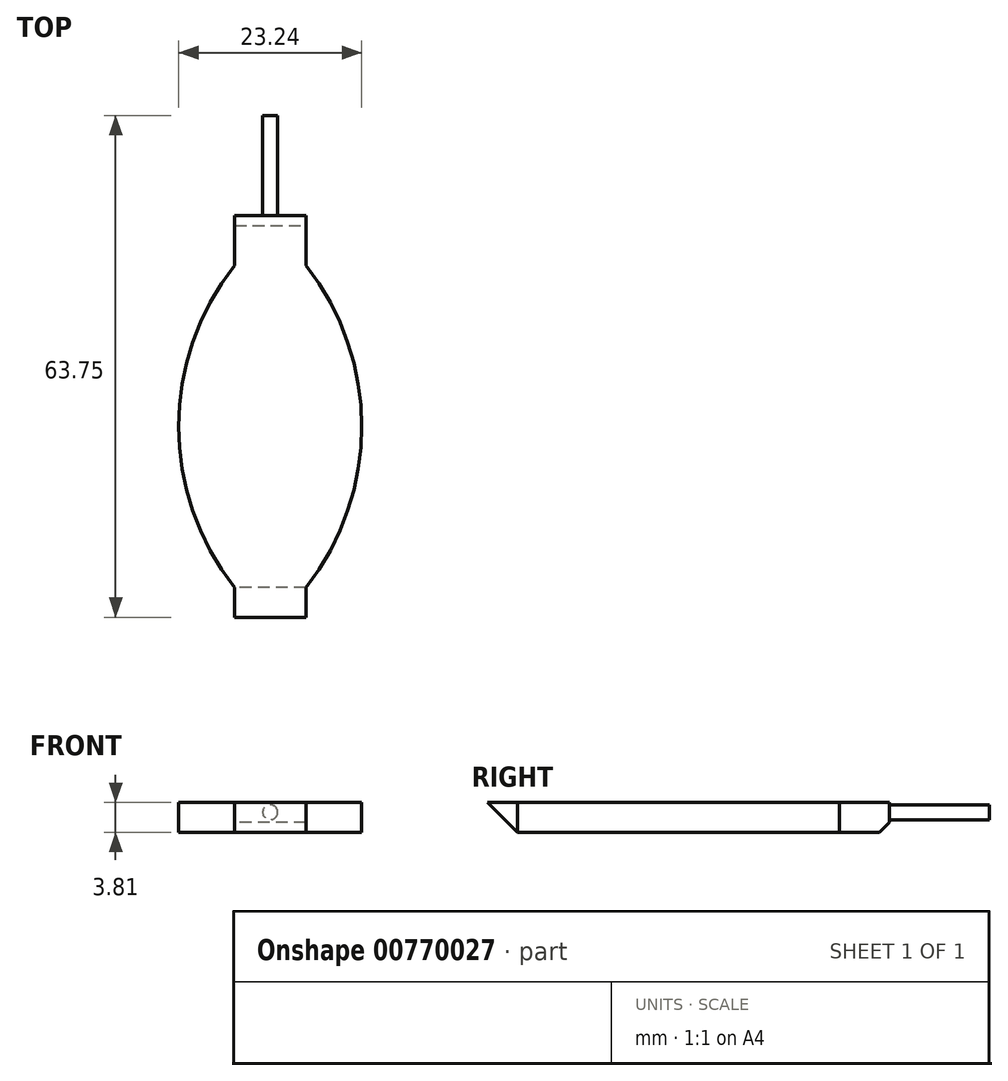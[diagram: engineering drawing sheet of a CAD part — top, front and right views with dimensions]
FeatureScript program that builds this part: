
annotation { "Feature Type Name" : "Feature", "Feature Type Description" : "" }
export const myFeature = defineFeature(function(context is Context, id is Id, definition is map)
    precondition{}
    {
        {
            var Q0;
            Q0=qCreatedBy(makeId("Top.planeOp"),FACE);
            var sketch = newSketch(context, id + "F0", { "sketchPlane" : qUnion([Q0])});
            skLineSegment(sketch, "E0.top", {"start": v(-4.53, -2.42) * mm, "end": v(4.53, -2.42) * mm});
            skPoint(sketch, "E0.middle", {"position": v(0, 0) * mm});
            skLineSegment(sketch, "E1", {"start": v(-4.53, -43.3) * mm, "end": v(4.53, -43.3) * mm});
            skArc(sketch, "E2", {"start": v(4.53, -43.3) * mm, "mid": v(11.62, -22.86) * mm, "end": v(4.53, -2.42) * mm});
            skArc(sketch, "E3", {"start": v(-4.53, -2.42) * mm, "mid": v(-11.62, -22.86) * mm, "end": v(-4.53, -43.3) * mm});
            skSolve(sketch);
        }
        {
            var Q0;
            Q0=qSketchRegion(id+"F0",true);
            extrude(context, id + "F1", {"entities" : qUnion([Q0]), "depth" : 3.8 * mm, "offsetDistance" : 25.4 * mm});
        }
        {
            var Q0;
            Q0=makeQuery(id+"F1.opExtrude","SWEPT_FACE",FACE,{"disambiguationData":[OSD([sQuery(id+"F0.wireOp",EDGE,"E0.top")])]});
            var sketch = newSketch(context, id + "F2", { "sketchPlane" : qUnion([Q0])});
            skLineSegment(sketch, "E4.bottom", {"start": v(-4.53, 3.81) * mm, "end": v(4.53, 3.81) * mm});
            skLineSegment(sketch, "E4.top", {"start": v(-4.53, 0) * mm, "end": v(4.53, 0) * mm});
            skLineSegment(sketch, "E4.left", {"start": v(-4.53, 3.81) * mm, "end": v(-4.53, 0) * mm});
            skLineSegment(sketch, "E4.right", {"start": v(4.53, 3.81) * mm, "end": v(4.53, 0) * mm});
            skSolve(sketch);
        }
        {
            var Q0;
            Q0=qSketchRegion(id+"F2",true);
            extrude(context, id + "F3", {"entities" : qUnion([Q0]), "operationType" : NewBodyOperationType.ADD, "depth" : 6.35 * mm, "offsetDistance" : 25.4 * mm});
        }
        {
            var Q0;
            Q0=makeQuery(id+"F3.opExtrude","CAP_EDGE",EDGE,{"disambiguationData":[OSD([sQuery(id+"F2.wireOp",EDGE,"E4.top")])],"isStart":false});
            chamfer(context, id + "F4", {"entities" : qUnion([Q0]), "width" : 1.27 * mm, "tangentPropagation" : true});
        }
        {
            var Q0;
            Q0=makeQuery(id+"F1.opExtrude","SWEPT_FACE",FACE,{"disambiguationData":[OSD([sQuery(id+"F0.wireOp",EDGE,"E1")])]});
            var sketch = newSketch(context, id + "F5", { "sketchPlane" : qUnion([Q0])});
            skLineSegment(sketch, "E5.bottom", {"start": v(-4.53, 3.81) * mm, "end": v(4.53, 3.81) * mm});
            skLineSegment(sketch, "E5.top", {"start": v(-4.53, 0) * mm, "end": v(4.53, 0) * mm});
            skLineSegment(sketch, "E5.left", {"start": v(-4.53, 3.81) * mm, "end": v(-4.53, 0) * mm});
            skLineSegment(sketch, "E5.right", {"start": v(4.53, 3.81) * mm, "end": v(4.53, 0) * mm});
            skSolve(sketch);
        }
        {
            var Q0;
            Q0=qSketchRegion(id+"F5",true);
            extrude(context, id + "F6", {"entities" : qUnion([Q0]), "operationType" : NewBodyOperationType.ADD, "depth" : 5.08 * mm, "offsetDistance" : 25.4 * mm});
        }
        {
            var Q0;
            Q0=makeQuery(id+"F6.opExtrude","CAP_EDGE",EDGE,{"disambiguationData":[OSD([sQuery(id+"F5.wireOp",EDGE,"E5.top")])],"isStart":false});
            chamfer(context, id + "F7", {"entities" : qUnion([Q0]), "width" : 5.08 * mm, "tangentPropagation" : true});
        }
        {
            var Q0;
            Q0=makeQuery(id+"F3.opExtrude","CAP_FACE",FACE,{"disambiguationData":[OSD([sQuery(id+"F2.wireOp",EDGE,"E4.bottom"),sQuery(id+"F2.wireOp",EDGE,"E4.top"),sQuery(id+"F2.wireOp",EDGE,"E4.left"),sQuery(id+"F2.wireOp",EDGE,"E4.right")])],"isStart":false});
            var sketch = newSketch(context, id + "F8", { "sketchPlane" : qUnion([Q0])});
            skCircle(sketch, "E6", {"center": v(0, 2.55) * mm, "radius": 0.95 * mm});
            skPoint(sketch, "E6.centerSnap0", {"position": v(0, 1.27) * mm});
            skSolve(sketch);
        }
        {
            var Q0;
            Q0 = qSketchRegion(id + "F8", true);
            extrude(context, id + "F9", {"entities" : qUnion([Q0]), "operationType" : NewBodyOperationType.ADD, "depth" : 12.7 * mm, "offsetDistance" : 25.4 * mm});
        }
    });
